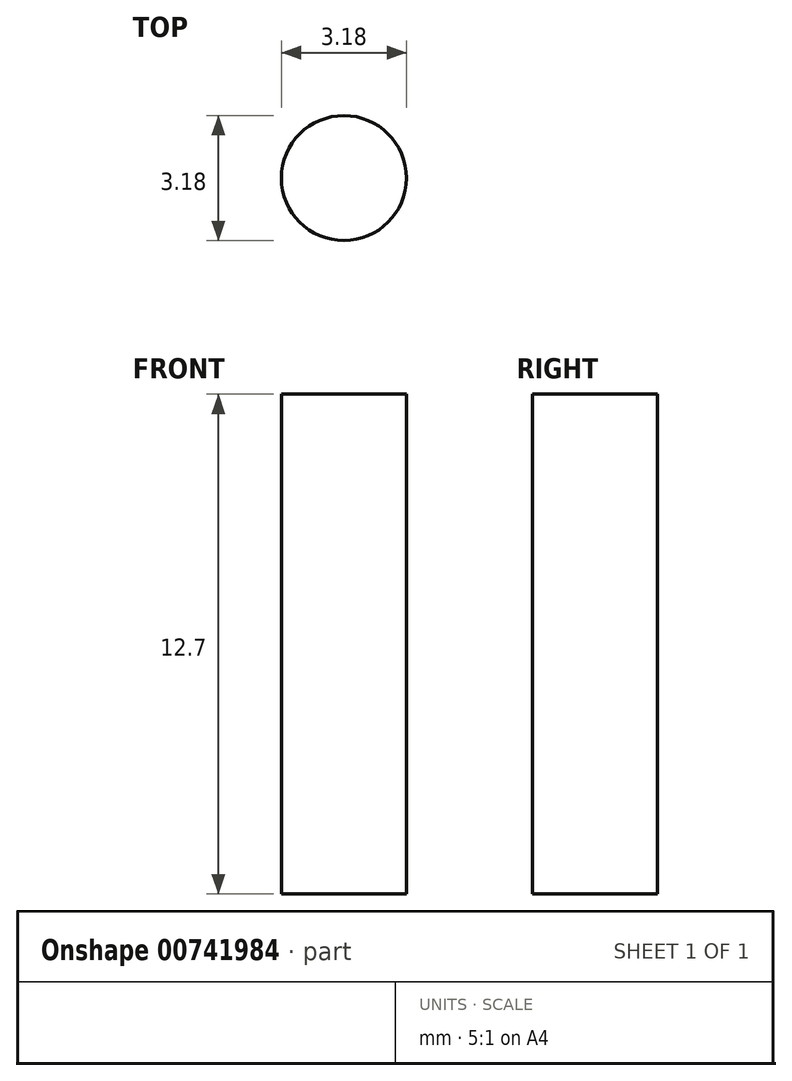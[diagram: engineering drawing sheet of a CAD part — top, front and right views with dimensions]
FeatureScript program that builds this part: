
annotation { "Feature Type Name" : "Feature", "Feature Type Description" : "" }
export const myFeature = defineFeature(function(context is Context, id is Id, definition is map)
    precondition{}
    {
        {
            var Q0;
            Q0=qCreatedBy(makeId("Top.planeOp"),FACE);
            var sketch = newSketch(context, id + "F0", { "sketchPlane" : qUnion([Q0])});
            skCircle(sketch, "E0", {"center": v(0, 0) * mm, "radius": 1.59 * mm});
            skSolve(sketch);
        }
        {
            var Q0;
            Q0 = qSketchRegion(id + "F0", true);
            extrude(context, id + "F1", {"entities" : qUnion([Q0]), "depth" : 12.7 * mm, "offsetDistance" : 25.4 * mm});
        }
    });
